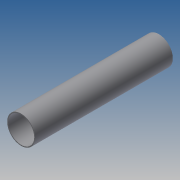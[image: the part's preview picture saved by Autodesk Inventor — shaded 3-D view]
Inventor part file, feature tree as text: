
AUTODESK INVENTOR PART (.ipt)
format: ipt  version: 2014 SP1 (Build 180222100, 222)  size: 77,312 bytes
history: native  units: in
note: dims shown in document units (in); Inventor stores cm internally (conversion verified against a paired STEP export)
features: extrude x1, sketch x1
ambient origin geometry x8: Origin, YZ Plane, XZ Plane, XY Plane, X Axis, Y Axis, Z Axis, Center Point
bodies: Solid1 (feature_tree)
feature tree (2):
  extrude  "Extrusion1"  Depth=29.5276in
  sketch  "Sketch1"  dims[d1=0.2in d2=6.0in d3=29.5276in d4=0.0in]
